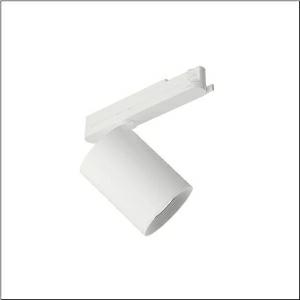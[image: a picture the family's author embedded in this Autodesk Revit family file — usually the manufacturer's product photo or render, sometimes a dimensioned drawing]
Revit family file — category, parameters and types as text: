
# Revit family: spot_21_51se14mba5b
name_source: partatom
category: Lighting Fixtures
units: mm (PartAtom-declared; Revit-internal decimal feet)

## family parameters
Cut with Voids When Loaded = No
Host = Face
Light Source = No
Part Type = Normal
Room Calculation Point = No
Round Connector Dimension = Use Diameter
Shared = No

## types (1)
- --- (1 x LED, 5340 lm, 41.8 W, 2700K)
    Apparent Load = 42 VA
    CIE Flux Codes = 96 99 100 100 100
    Color Rendering = 90
    Color Temperature = 2700K
    Default Elevation = 1800 mm
    Description = Spot 21, directional spotlight, light control with lens, of PMMA, LED rated luminous flux: 5.030lm, light colour: 927, control gear: ECG Multilumen, with 3-phase adapter, mains connection: 220..240V, AC, 50/60Hz, of aluminium, traffic white (RAL 9016), length: 213mm, diameter: 105mm, protection rating (complete): IP20, insulation class (complete): insulation class I (protective earthing), certification: CE, impact resistance: IK02, permissible ambient temperature for indoor applications: -20..+40°C, packaging unit: 1 piece
    Height = 175 mm
    Lamp = 1 x LED
    Lamp Light Flux = 5340 lm
    Lamp Power = 41.8 W
    Lamp count = 1
    Length = 105 mm
    Luminous efficacy = 128 lm/W
    Manufacturer = Siteco
    ModVariant = No
    Model = 51SE14MBA5B
    Mounting Place = Ceiling
    Mounting Type = Pendant
    Number of Poles = 1
    OnlyDefault = Yes
    Power Factor = 1
    Product Name = Spot 21
    Product group = directional spotlight
    ProductGroupID = 905
    Protection Class = Protection class I
    Protection Degree = IP 20
    RLX_Detail_Level = 1
    RLX_Emergency_Light_Flux = 0 lm
    RLX_Emergency_Type = 0
    RLX_Emergency_Type_DB = No
    RlxData = <blob elided: 17625 chars, md5=c22eb8da>
    Socket = socket
    Standby Power = 0 W
    System Light Flux = 5340 lm
    System Power = 42 W
    Type Comments = factory setting: luminous flux: 100 % | (ON | ON | ON | ON) | 1050 mA
    Type Image = l_1003976.jpg
    URL = http://relux.com
    VarID = @adj_164929
    Voltage = 0 V
    Weight = 0.00 kg
    Width = 0 mm  [stored 0 ft]

note: [stored X ft] marks values corroborated as IEEE doubles in the binary element streams (Revit-internal decimal feet)

## geometry (parser evidence)
native form markers: Blend x4, Sweep x9
no freeform markers — native parametric forms only
